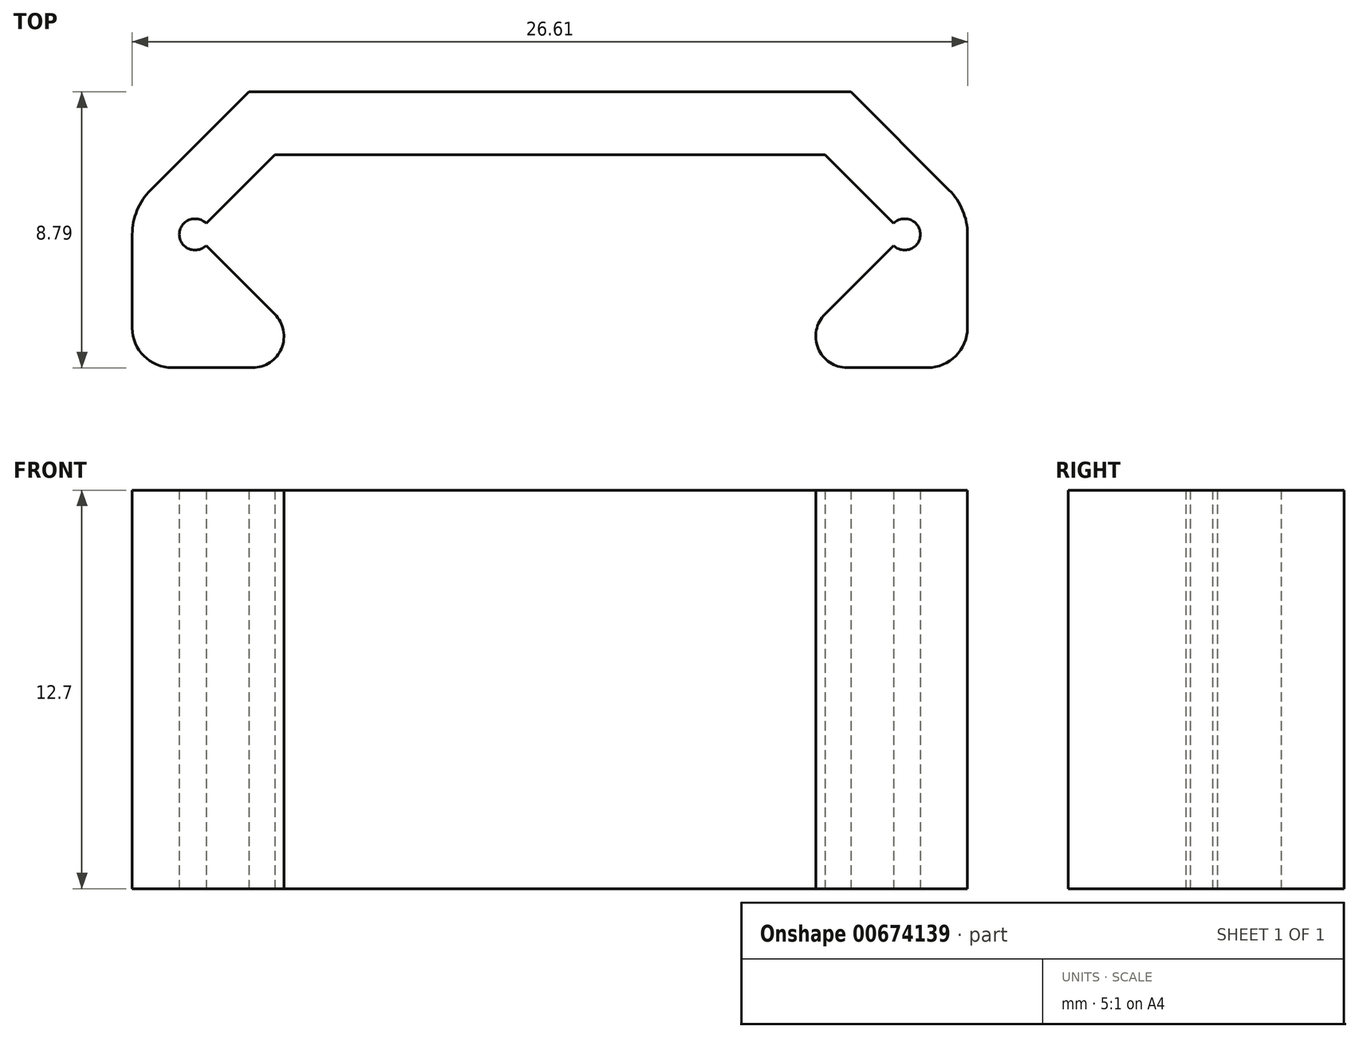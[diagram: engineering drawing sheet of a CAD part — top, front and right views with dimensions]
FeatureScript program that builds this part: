
annotation { "Feature Type Name" : "Feature", "Feature Type Description" : "" }
export const myFeature = defineFeature(function(context is Context, id is Id, definition is map)
    precondition{}
    {
        {
            var Q0;
            Q0=qCreatedBy(makeId("Top.planeOp"),FACE);
            var sketch = newSketch(context, id + "F0", { "sketchPlane" : qUnion([Q0])});
            skLineSegment(sketch, "E0.top", {"start": v(0.35, 0.35) * mm, "end": v(2.54, 2.54) * mm});
            skLineSegment(sketch, "E0.left", {"start": v(2.54, -2.54) * mm, "end": v(0.35, -0.35) * mm});
            skLineSegment(sketch, "E1.top", {"start": v(20.07, 2.54) * mm, "end": v(22.25, 0.35) * mm});
            skLineSegment(sketch, "E1.right", {"start": v(20.07, -2.54) * mm, "end": v(22.25, -0.35) * mm});
            skLineSegment(sketch, "E2.2", {"start": v(-1.41, 1.41) * mm, "end": v(1.71, 4.54) * mm});
            skLineSegment(sketch, "E2.4", {"start": v(20.9, 4.54) * mm, "end": v(24.02, 1.41) * mm});
            skArc(sketch, "E3", {"start": v(0.35, 0.35) * mm, "mid": v(-0.5, 0) * mm, "end": v(0.35, -0.35) * mm});
            skArc(sketch, "E4", {"start": v(22.25, -0.35) * mm, "mid": v(23.1, 0) * mm, "end": v(22.25, 0.35) * mm});
            skArc(sketch, "E5", {"start": v(24.6, 0) * mm, "mid": v(24.45, 0.77) * mm, "end": v(24.02, 1.41) * mm});
            skArc(sketch, "E6", {"start": v(-1.41, 1.41) * mm, "mid": v(-1.85, 0.77) * mm, "end": v(-2, 0) * mm});
            skArc(sketch, "E7", {"start": v(1.83, -4.25) * mm, "mid": v(2.76, -3.63) * mm, "end": v(2.54, -2.54) * mm});
            skArc(sketch, "E8", {"start": v(20.07, -2.54) * mm, "mid": v(19.85, -3.63) * mm, "end": v(20.77, -4.25) * mm});
            skLineSegment(sketch, "E9", {"start": v(1.83, -4.25) * mm, "end": v(-0.73, -4.25) * mm});
            skLineSegment(sketch, "E10", {"start": v(20.77, -4.25) * mm, "end": v(23.34, -4.25) * mm});
            skLineSegment(sketch, "E11", {"start": v(-2, 0) * mm, "end": v(-2, -2.98) * mm});
            skLineSegment(sketch, "E12", {"start": v(24.6, 0) * mm, "end": v(24.6, -2.98) * mm});
            skPoint(sketch, "E2.1.start.orphan", {"position": v(1.13, -3.95) * mm});
            skPoint(sketch, "E13.orphan", {"position": v(21.48, -3.95) * mm});
            skPoint(sketch, "E14.visualSharp", {"position": v(-2, -4.25) * mm});
            skArc(sketch, "E14.filletArc", {"start": v(-2, -2.98) * mm, "mid": v(-1.63, -3.88) * mm, "end": v(-0.73, -4.25) * mm});
            skPoint(sketch, "E15.visualSharp", {"position": v(24.6, -4.25) * mm});
            skArc(sketch, "E15.filletArc", {"start": v(23.34, -4.25) * mm, "mid": v(24.23, -3.88) * mm, "end": v(24.6, -2.98) * mm});
            skLineSegment(sketch, "E16", {"start": v(11.7, 2.54) * mm, "end": v(20.07, 2.54) * mm});
            skLineSegment(sketch, "E17", {"start": v(11.7, 2.54) * mm, "end": v(2.54, 2.54) * mm});
            skLineSegment(sketch, "E18.0", {"start": v(11.7, 4.54) * mm, "end": v(1.71, 4.54) * mm});
            skLineSegment(sketch, "E18.1", {"start": v(11.7, 4.54) * mm, "end": v(20.9, 4.54) * mm});
            skSolve(sketch);
        }
        {
            var Q0;
            Q0 = qSketchRegion(id + "F0", true);
            extrude(context, id + "F1", {"entities" : qUnion([Q0]), "depth" : 12.7 * mm, "offsetDistance" : 25.4 * mm});
        }
    });
